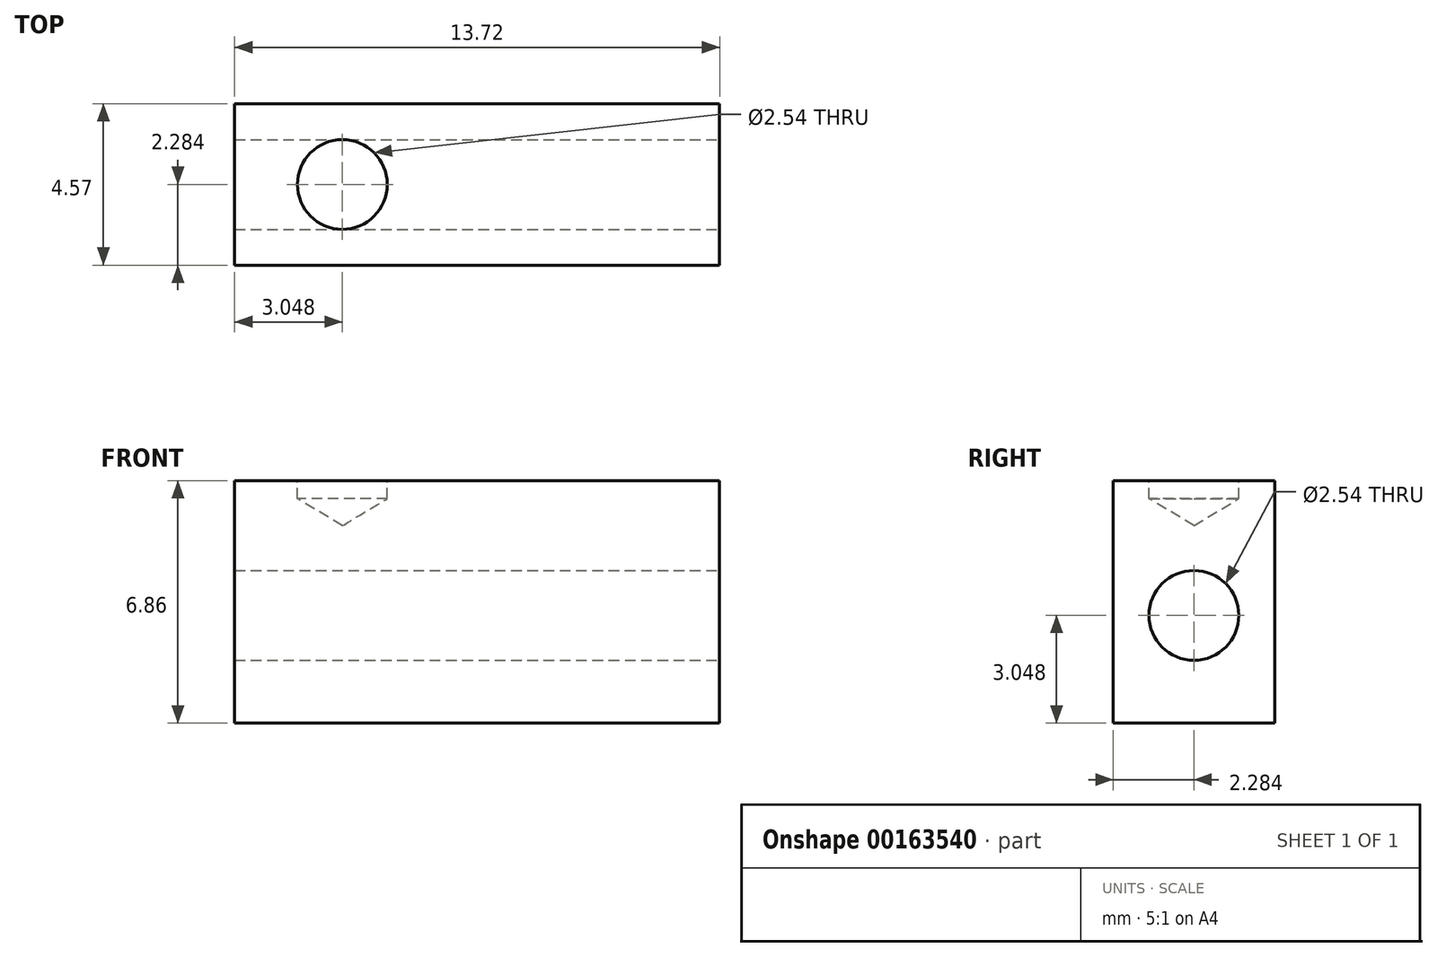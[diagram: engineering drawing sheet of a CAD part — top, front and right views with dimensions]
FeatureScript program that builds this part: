
annotation { "Feature Type Name" : "Feature", "Feature Type Description" : "" }
export const myFeature = defineFeature(function(context is Context, id is Id, definition is map)
    precondition{}
    {
        {
            var Q0;
            Q0=qCreatedBy(makeId("Front.planeOp"),FACE);
            var sketch = newSketch(context, id + "F0", { "sketchPlane" : qUnion([Q0])});
            skLineSegment(sketch, "E0.bottom", {"start": v(0, 0) * mm, "end": v(13.72, 0) * mm});
            skLineSegment(sketch, "E0.top", {"start": v(0, 6.86) * mm, "end": v(13.72, 6.86) * mm});
            skLineSegment(sketch, "E0.left", {"start": v(0, 0) * mm, "end": v(0, 6.86) * mm});
            skLineSegment(sketch, "E0.right", {"start": v(13.72, 0) * mm, "end": v(13.72, 6.86) * mm});
            skSolve(sketch);
        }
        {
            var Q0;
            Q0 = qSketchRegion(id + "F0", true);
            extrude(context, id + "F1", {"entities" : qUnion([Q0]), "depth" : 4.57 * mm});
        }
        {
            var Q0;
            Q0=makeQuery(id+"F1.opExtrude","SWEPT_FACE",FACE,{"disambiguationData":[OSD([sQuery(id+"F0.wireOp",EDGE,"E0.right")])]});
            var sketch = newSketch(context, id + "F2", { "sketchPlane" : qUnion([Q0])});
            skCircle(sketch, "E1", {"center": v(-2.29, 3.05) * mm, "radius": 1.42 * mm});
            skSolve(sketch);
        }
        {
            var Q0;
            Q0=sQuery(id+"F2.wireOp",VERTEX,"E1.center");
            var Q1;
            Q1=makeQuery(id+"F1.opExtrude","SWEPT_BODY",BODY,{"disambiguationData":[OSD([sQuery(id+"F0.wireOp",EDGE,"E0.bottom"),sQuery(id+"F0.wireOp",EDGE,"E0.top"),sQuery(id+"F0.wireOp",EDGE,"E0.left"),sQuery(id+"F0.wireOp",EDGE,"E0.right")])]});
            hole(context, id + "F3", {"style" : HoleStyle.SIMPLE, "endStyle" : HoleEndStyle.THROUGH, "holeDiameter" : 2.54 * mm, "locations" : qUnion([Q0]), "scope" : qUnion([Q1]), "isTappedThrough" : true});
        }
        {
            var Q0;
            Q0=makeQuery(id+"F1.opExtrude","SWEPT_FACE",FACE,{"disambiguationData":[OSD([sQuery(id+"F0.wireOp",EDGE,"E0.top")])]});
            var sketch = newSketch(context, id + "F4", { "sketchPlane" : qUnion([Q0])});
            skCircle(sketch, "E2", {"center": v(3.05, -2.29) * mm, "radius": 1.04 * mm});
            skSolve(sketch);
        }
        {
            var Q0;
            Q0=sQuery(id+"F4.wireOp",VERTEX,"E2.center");
            var Q1;
            Q1=makeQuery(id+"F1.opExtrude","SWEPT_BODY",BODY,{"disambiguationData":[OSD([sQuery(id+"F0.wireOp",EDGE,"E0.bottom"),sQuery(id+"F0.wireOp",EDGE,"E0.top"),sQuery(id+"F0.wireOp",EDGE,"E0.left"),sQuery(id+"F0.wireOp",EDGE,"E0.right")])]});
            hole(context, id + "F5", {"style" : HoleStyle.SIMPLE, "endStyle" : HoleEndStyle.BLIND, "holeDiameter" : 2.54 * mm, "holeDepth" : 0.5 * mm, "locations" : qUnion([Q0]), "scope" : qUnion([Q1])});
        }
    });
